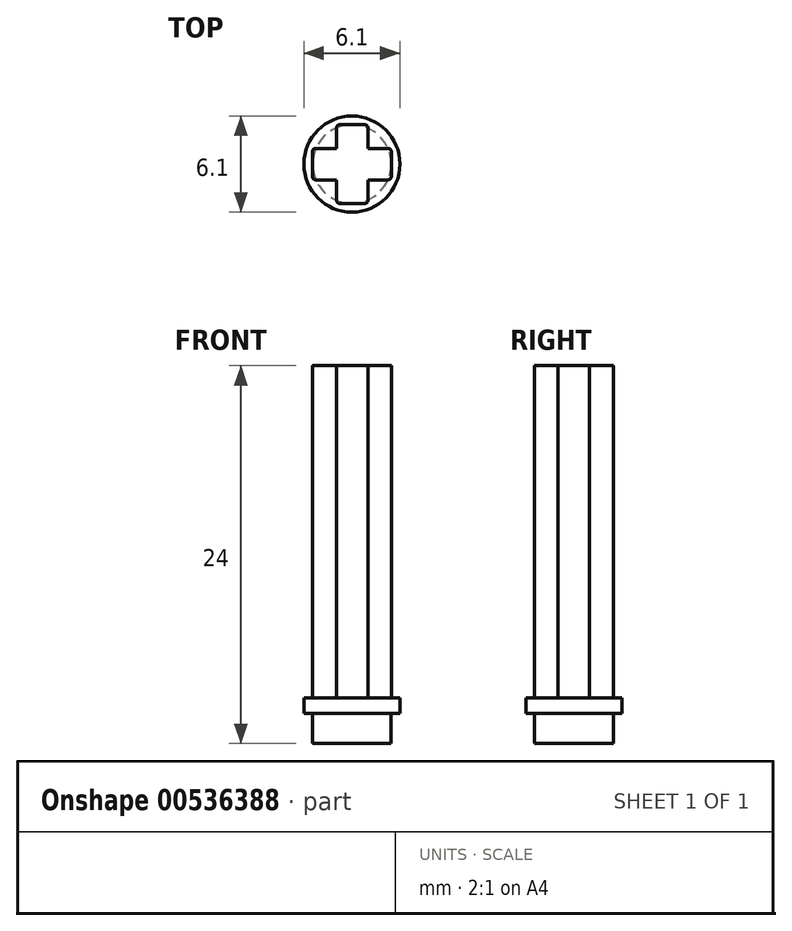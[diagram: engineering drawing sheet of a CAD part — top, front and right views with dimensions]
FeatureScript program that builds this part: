
annotation { "Feature Type Name" : "Feature", "Feature Type Description" : "" }
export const myFeature = defineFeature(function(context is Context, id is Id, definition is map)
    precondition{}
    {
        {
            var Q0;
            Q0=qCreatedBy(makeId("Top.planeOp"),FACE);
            var sketch = newSketch(context, id + "F0", { "sketchPlane" : qUnion([Q0])});
            skLineSegment(sketch, "E0.bottom", {"start": v(-17.82, 22.13) * mm, "end": v(-12.82, 22.13) * mm});
            skLineSegment(sketch, "E0.top", {"start": v(-17.82, 20.13) * mm, "end": v(-12.82, 20.13) * mm});
            skLineSegment(sketch, "E0.left", {"start": v(-17.82, 22.13) * mm, "end": v(-17.82, 20.13) * mm});
            skLineSegment(sketch, "E0.right", {"start": v(-12.82, 22.13) * mm, "end": v(-12.82, 20.13) * mm});
            skLineSegment(sketch, "E1.bottom", {"start": v(-16.3, 23.63) * mm, "end": v(-14.3, 23.63) * mm});
            skLineSegment(sketch, "E1.top", {"start": v(-16.3, 18.63) * mm, "end": v(-14.3, 18.63) * mm});
            skLineSegment(sketch, "E1.left", {"start": v(-16.3, 23.63) * mm, "end": v(-16.3, 18.63) * mm});
            skLineSegment(sketch, "E1.right", {"start": v(-14.3, 23.63) * mm, "end": v(-14.3, 18.63) * mm});
            skSolve(sketch);
        }
        {
            var Q0;
            Q0 = qSketchRegion(id + "F0", true);
            extrude(context, id + "F1", {"entities" : qUnion([Q0]), "depth" : 21.1 * mm, "offsetDistance" : 25 * mm});
        }
        {
            var Q0;
            Q0=qCreatedBy(makeId("Top.planeOp"),FACE);
            var sketch = newSketch(context, id + "F2", { "sketchPlane" : qUnion([Q0])});
            skCircle(sketch, "E2", {"center": v(-15.32, 21.13) * mm, "radius": 3.05 * mm});
            skSolve(sketch);
        }
        {
            var Q0;
            Q0=makeQuery(id+"F2.imprint","IMPRINT",FACE,{"disambiguationData":[TD([[makeQuery(id+"F2.imprint","IMPRINT",EDGE,{"derivedFrom":sQuery(id+"F2.wireOp",EDGE,"E2")}),1.0]])]});
            extrude(context, id + "F3", {"entities" : qUnion([Q0]), "operationType" : NewBodyOperationType.ADD, "oppositeDirection" : true, "depth" : 1 * mm, "offsetDistance" : 25 * mm});
        }
        {
            var Q0;
            Q0=makeQuery(id+"F3.opExtrude","CAP_FACE",FACE,{"disambiguationData":[OSD([sQuery(id+"F2.wireOp",EDGE,"E2")])],"isStart":false});
            var sketch = newSketch(context, id + "F4", { "sketchPlane" : qUnion([Q0])});
            skCircle(sketch, "E3", {"center": v(-15.32, -21.13) * mm, "radius": 2.5 * mm});
            skSolve(sketch);
        }
        {
            var Q0;
            Q0 = qSketchRegion(id + "F4", true);
            extrude(context, id + "F5", {"entities" : qUnion([Q0]), "operationType" : NewBodyOperationType.ADD, "depth" : 1.9 * mm, "offsetDistance" : 25 * mm});
        }
        {
            var Q0;
            Q0=makeQuery(id+"F1.opExtrude","SWEPT_EDGE",EDGE,{"disambiguationData":[OSD([sQuery(id+"F0.wireOp",EDGE,"E0.top"),sQuery(id+"F0.wireOp",EDGE,"E0.right")])]});
            var Q1;
            Q1=makeQuery(id+"F1.opExtrude","SWEPT_EDGE",EDGE,{"disambiguationData":[OSD([sQuery(id+"F0.wireOp",EDGE,"E0.bottom"),sQuery(id+"F0.wireOp",EDGE,"E0.right")])]});
            var Q2;
            Q2=makeQuery(id+"F1.opExtrude","SWEPT_EDGE",EDGE,{"disambiguationData":[OSD([sQuery(id+"F0.wireOp",EDGE,"E1.top"),sQuery(id+"F0.wireOp",EDGE,"E1.right")])]});
            var Q3;
            Q3=makeQuery(id+"F1.opExtrude","SWEPT_EDGE",EDGE,{"disambiguationData":[OSD([sQuery(id+"F0.wireOp",EDGE,"E1.top"),sQuery(id+"F0.wireOp",EDGE,"E1.left")])]});
            var Q4;
            Q4=makeQuery(id+"F1.opExtrude","SWEPT_EDGE",EDGE,{"disambiguationData":[OSD([sQuery(id+"F0.wireOp",EDGE,"E0.top"),sQuery(id+"F0.wireOp",EDGE,"E0.left")])]});
            var Q5;
            Q5=makeQuery(id+"F1.opExtrude","SWEPT_EDGE",EDGE,{"disambiguationData":[OSD([sQuery(id+"F0.wireOp",EDGE,"E0.bottom"),sQuery(id+"F0.wireOp",EDGE,"E0.left")])]});
            var Q6;
            Q6=makeQuery(id+"F1.opExtrude","SWEPT_EDGE",EDGE,{"disambiguationData":[OSD([sQuery(id+"F0.wireOp",EDGE,"E1.bottom"),sQuery(id+"F0.wireOp",EDGE,"E1.left")])]});
            var Q7;
            Q7=makeQuery(id+"F1.opExtrude","SWEPT_EDGE",EDGE,{"disambiguationData":[OSD([sQuery(id+"F0.wireOp",EDGE,"E1.bottom"),sQuery(id+"F0.wireOp",EDGE,"E1.right")])]});
            fillet(context, id + "F6", {"entities" : qUnion([Q0, Q1, Q2, Q3, Q4, Q5, Q6, Q7]), "radius" : 0.2 * mm, "tangentPropagation" : true, "allowEdgeOverflow" : false});
        }
    });
